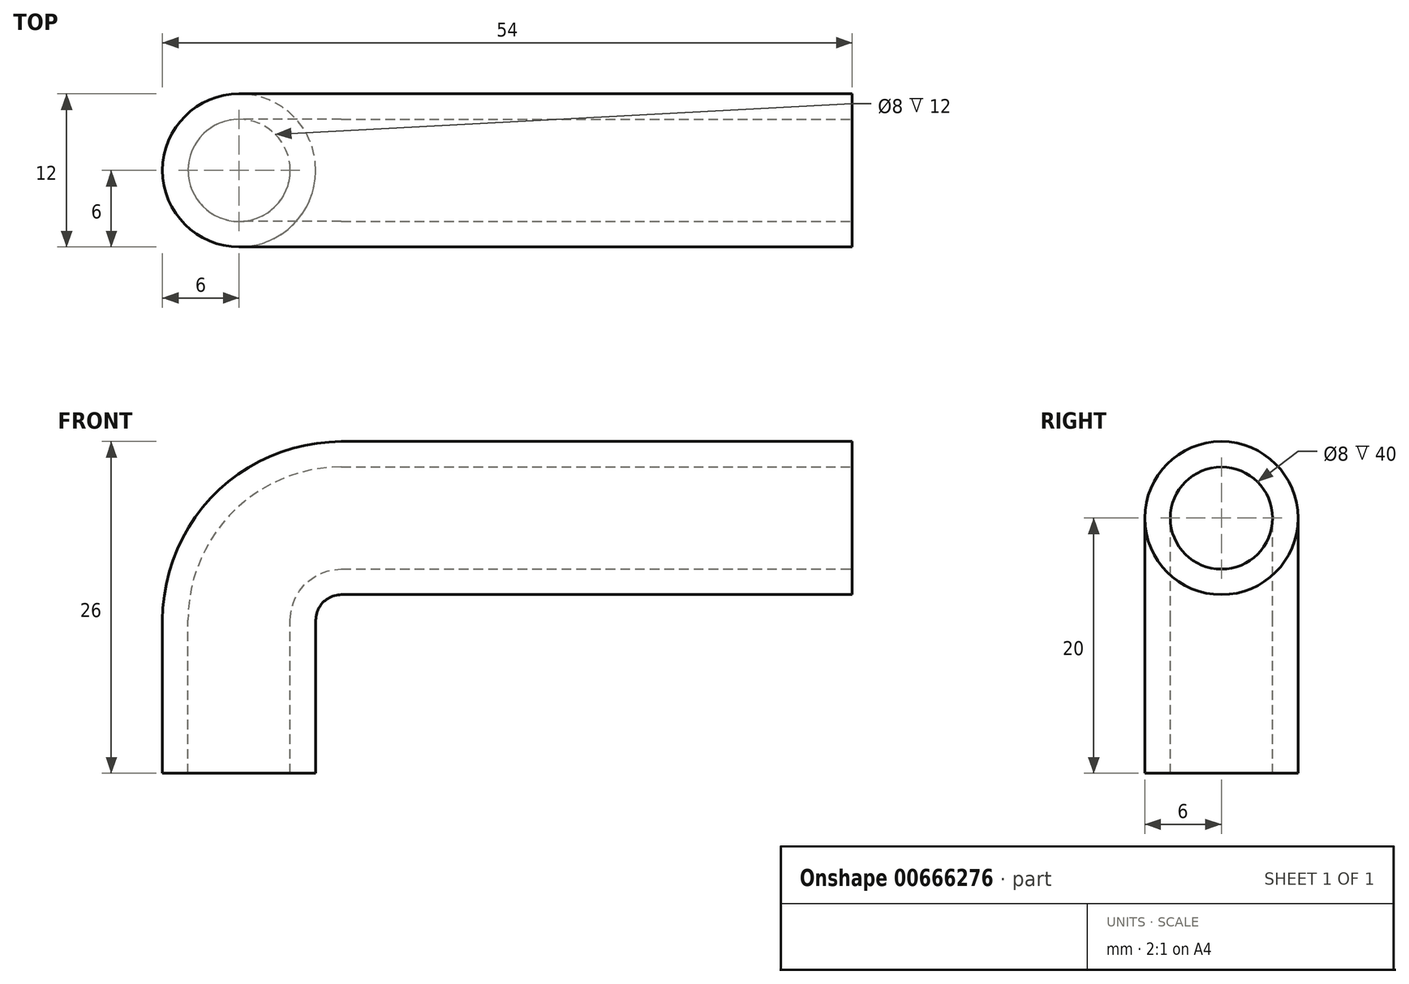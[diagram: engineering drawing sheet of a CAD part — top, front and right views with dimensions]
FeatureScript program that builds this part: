
annotation { "Feature Type Name" : "Feature", "Feature Type Description" : "" }
export const myFeature = defineFeature(function(context is Context, id is Id, definition is map)
    precondition{}
    {
        {
            var Q0;
            Q0=qCreatedBy(makeId("Front.planeOp"),FACE);
            var sketch = newSketch(context, id + "F0", { "sketchPlane" : qUnion([Q0])});
            skLineSegment(sketch, "E0", {"start": v(0, 0) * mm, "end": v(0, 12) * mm});
            skLineSegment(sketch, "E1", {"start": v(8, 20) * mm, "end": v(48, 20) * mm});
            skArc(sketch, "E2", {"start": v(8, 20) * mm, "mid": v(2.34, 17.66) * mm, "end": v(0, 12) * mm});
            skSolve(sketch);
        }
        {
            var Q0;
            Q0=qCreatedBy(makeId("Top.planeOp"),FACE);
            var sketch = newSketch(context, id + "F1", { "sketchPlane" : qUnion([Q0])});
            skCircle(sketch, "E3", {"center": v(0, 0) * mm, "radius": 4 * mm});
            skCircle(sketch, "E4", {"center": v(0, 0) * mm, "radius": 6 * mm});
            skSolve(sketch);
        }
        {
            var Q0;
            Q0=makeQuery(id+"F1.imprint","IMPRINT",FACE,{"disambiguationData":[TD([[makeQuery(id+"F1.imprint","IMPRINT",EDGE,{"derivedFrom":sQuery(id+"F1.wireOp",EDGE,"E3")}),-1.0]])]});
            var Q1;
            Q1=sQuery(id+"F0.wireOp",EDGE,"E0");
            var Q2;
            Q2=sQuery(id+"F0.wireOp",EDGE,"V2QttvWe-IFNE-IMvH-WZLn-VIeUTu6dHqql");
            var Q3;
            Q3=sQuery(id+"F0.wireOp",EDGE,"E2");
            var Q4;
            Q4=sQuery(id+"F0.wireOp",EDGE,"JWmf7mI7-Hcs9-otbt-b2Xv-1pcoOw7dfftm");
            var Q5;
            Q5=sQuery(id+"F0.wireOp",EDGE,"E1");
            sweep(context, id + "F2", {"profiles" : qUnion([Q0]), "path" : qUnion([Q1, Q2, Q3, Q4, Q5])});
        }
    });
